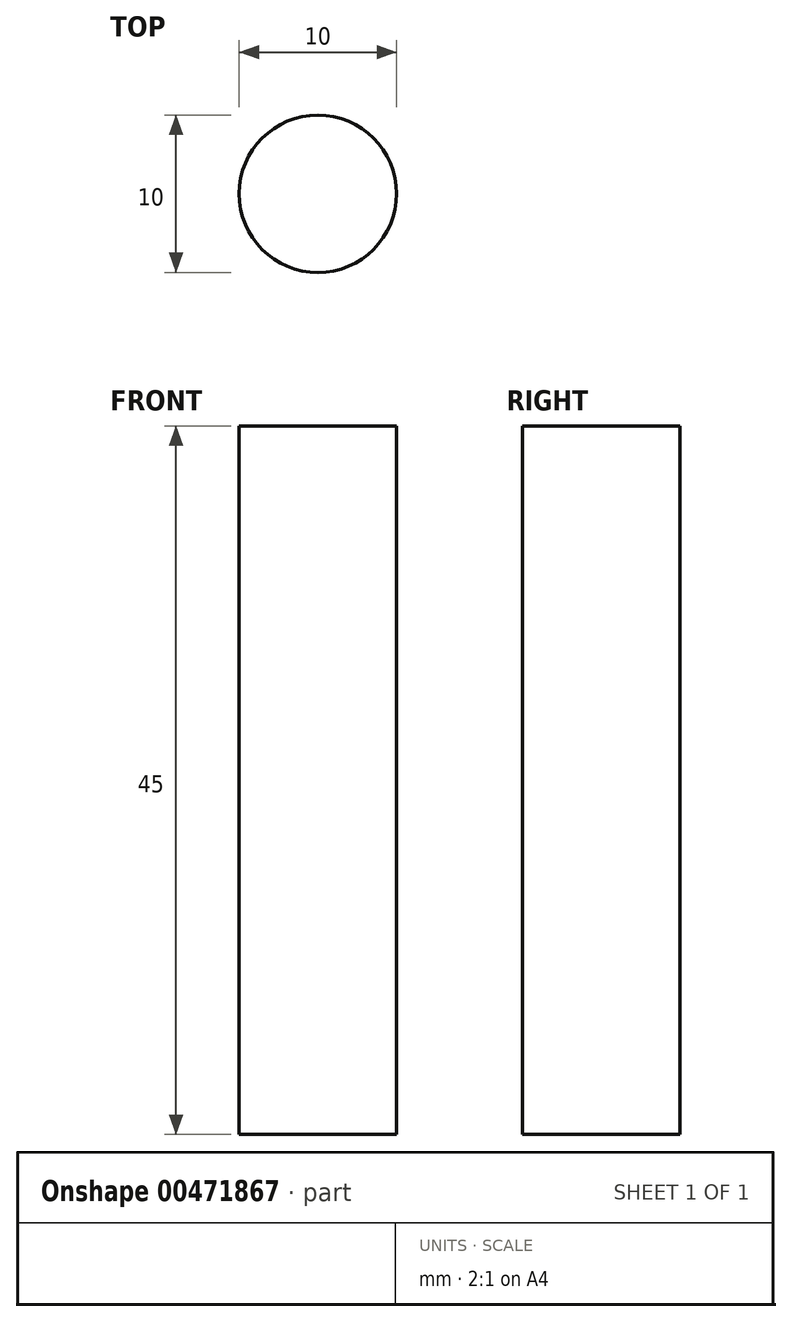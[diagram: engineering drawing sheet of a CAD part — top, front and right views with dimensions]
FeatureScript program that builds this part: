
annotation { "Feature Type Name" : "Feature", "Feature Type Description" : "" }
export const myFeature = defineFeature(function(context is Context, id is Id, definition is map)
    precondition{}
    {
        {
            var Q0;
            Q0=qCreatedBy(makeId("Front.planeOp"),FACE);
            var sketch = newSketch(context, id + "F0", { "sketchPlane" : qUnion([Q0])});
            skLineSegment(sketch, "E0", {"start": v(0, 0) * mm, "end": v(0, 49.29) * mm, "construction": true});
            skLineSegment(sketch, "E1.bottom", {"start": v(0, 0) * mm, "end": v(-5, 0) * mm});
            skLineSegment(sketch, "E1.top", {"start": v(0, 45) * mm, "end": v(-5, 45) * mm});
            skLineSegment(sketch, "E1.left", {"start": v(0, 0) * mm, "end": v(0, 45) * mm});
            skLineSegment(sketch, "E1.right", {"start": v(-5, 0) * mm, "end": v(-5, 45) * mm});
            skSolve(sketch);
        }
        {
            var Q0;
            Q0 = qSketchRegion(id + "F0", true);
            var Q1;
            Q1=sQuery(id+"F0.wireOp",EDGE,"E1.left");
            revolve(context, id + "F1", {"entities" : qUnion([Q0]), "axis" : qUnion([Q1]), "revolveType" : RevolveType.FULL});
        }
    });
